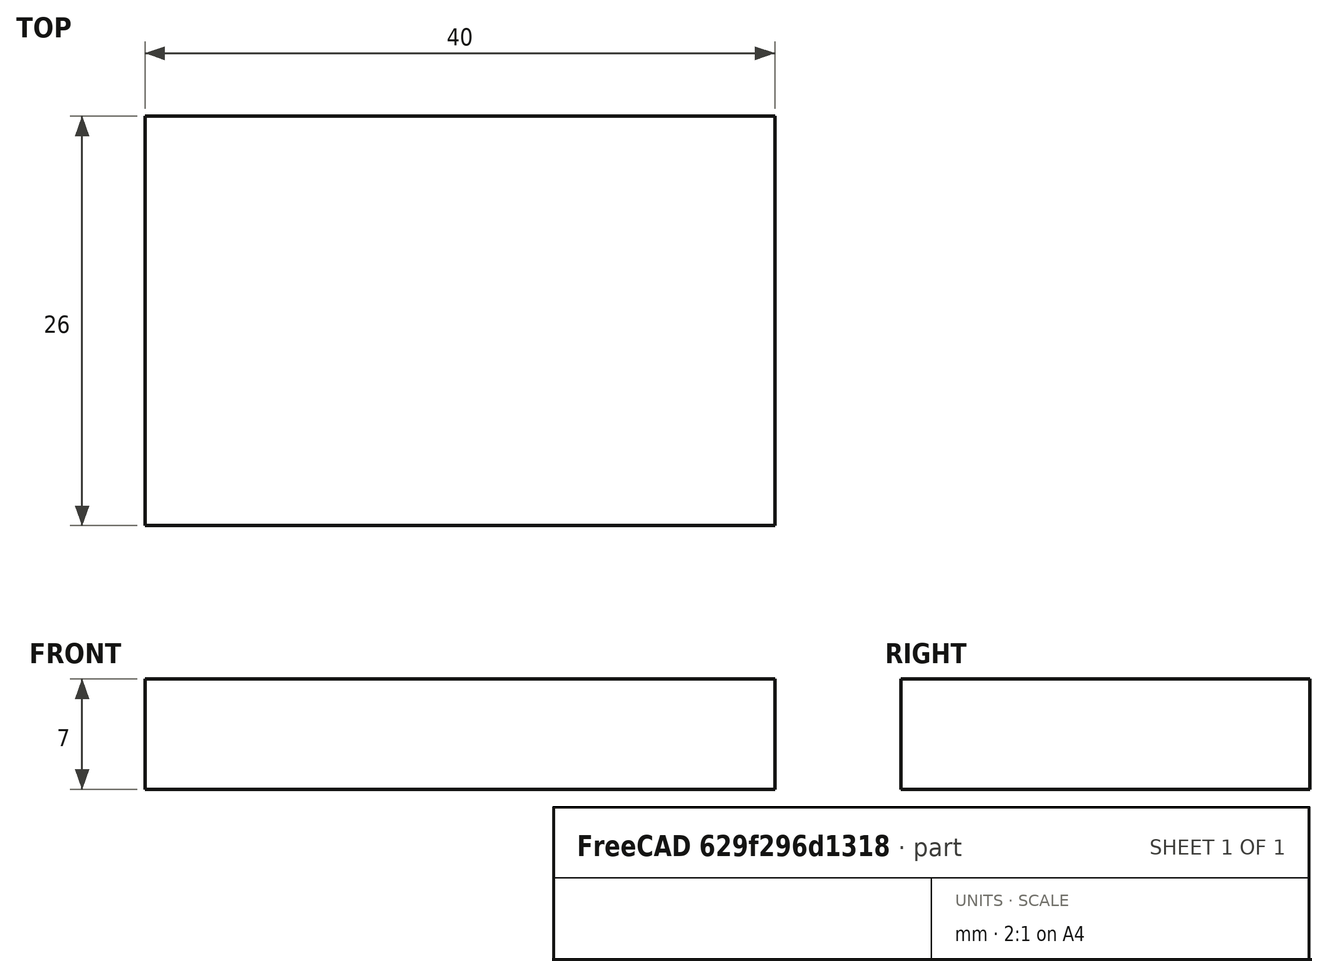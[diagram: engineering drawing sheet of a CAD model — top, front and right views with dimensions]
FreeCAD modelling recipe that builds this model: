
FCSTD DOCUMENT  (FreeCAD 0.17RUnknown)
Label: cam_tail
License: All rights reserved
LicenseURL: http://en.wikipedia.org/wiki/All_rights_reserved
objects: Path::FeaturePython×6, Part::FeaturePython×3, App::FeaturePython×1, Path::FeatureCompoundPython×1
note: 6 computed .brp shape members not serialized (recipe doc carries the construction recipe); baked Part::Feature solids carry a one-line shape summary decoded from their .brp

FEATURE [Path::FeaturePython] Default_Tool  label="Default Tool"  # Path/CAM operation (typed FeaturePython)
  HorizFeed = 3.33333
  HorizRapid = 0
  SpindleDir = 0
  SpindleSpeed = 12000
  ToolNumber = 1
  VertFeed = 1.33333
  VertRapid = 0
  expr: Tool.Diameter = 2
  expr: VertFeed = 80mm / min
  expr: HorizFeed = 200mm / min
  expr: HorizRapid = SetupSheet.HorizRapid
  expr: VertRapid = SetupSheet.VertRapid
FEATURE [Path::FeaturePython] Contour  # Path/CAM operation (typed FeaturePython)
  Active = true
  AreaParams:
    OpenMode = 0
    Angle = 45.0
    MinArcPoints = 4
    Coplanar = 2
    Tolerance = 1e-07
    CleanDistance = 0.0
    PocketExtraOffset = 0.0
    RoundPrecision = 0.0
    AngleShift = 0.0
    SubjectFill = 0
    PocketMode = 0
    Simplify = False
    SectionTolerance = 1e-06
    MaxArcPoints = 100
    Offset = 1.0
    Accuracy = 0.01
    PocketStepover = 0.0
    ClipFill = 0
    ToolRadius = 1.0
    Outline = False
    ClipperScale = 10000000.0
    FromCenter = False
    Explode = False
    EndType = 0
    Shift = 0.0
    ExtraPass = 0
    Project = False
    JoinType = 0
    Thicken = False
    Stepdown = 1.0
    SectionMode = 2
    MiterLimit = 2.0
    Deflection = 0.01
    Reorient = True
    FitArcs = True
    SectionCount = -1
    SectionOffset = 0.0
    Stepover = 0.0
    Unit = 1.0
    Fill = 0
  ClearanceHeight = 2
  Direction = 0
  FinalDepth = -6
  JoinType = 0
  MiterLimit = 0.1
  OffsetExtra = 0
  OpFinalDepth = -7
  OpStartDepth = 0
  OpToolDiameter = 2
  PathParams:
    resume_height = 2.0000000000000053
    feedrate = 3.3333333333333335
    verbose = True
    orientation = 1
    return_end = True
    preamble = False
    retraction = 2.0000000000000053
    feedrate_v = 1.3333333333333333
  SafeHeight = 2
  Side = 0
  StartDepth = 0
  StartPoint = (0,0,0)
  StepDown = 0.1
  ToolController = -> Default_Tool
  UseComp = true
  UseStartPoint = false
  expr: FinalDepth = -6
  expr: ClearanceHeight = StartDepth + SetupSheet.ClearanceHeightOffset
  expr: SafeHeight = StartDepth + SetupSheet.SafeHeightOffset
  expr: StepDown = 0.10000000000000001
  expr: StartDepth = OpStartDepth
FEATURE [App::FeaturePython] SetupSheet  # Path/CAM operation (typed FeaturePython)
  ClearanceHeightExpression = StartDepth+SetupSheet.ClearanceHeightOffset
  ClearanceHeightOffset = 2
  FinalDepthExpression = OpFinalDepth
  HorizRapid = 0
  SafeHeightExpression = StartDepth+SetupSheet.SafeHeightOffset
  SafeHeightOffset = 2
  StartDepthExpression = OpStartDepth
  StepDownExpression = OpToolDiameter
  VertRapid = 0
FEATURE [Part::FeaturePython] tail_01  # a2plus imported part (geometry in sourceFile) (typed FeaturePython)
  fixedPosition = true
  sourceFile = <userpath>/hs/fly/cad/tail.fcstd
  timeLastImport = 1.53696e+09
  updateColors = true
FEATURE [Part::FeaturePython] Clone  label="Base-arm_01"  # Draft clone (typed FeaturePython)
  AttacherType = Attacher::AttachEngine3D
  Fuse = false
  Objects = -> [tail_01]
  PathResource = Base
  Placement = pos=(21,17,-2.5) rot=(1,0,0;-1.5708rad)
  Scale = (1,1,1)
FEATURE [Path::FeaturePython] Pocket_Shape  # Path/CAM operation (typed FeaturePython)
  Active = true
  AreaParams:
    OpenMode = 0
    Angle = 45.0
    MinArcPoints = 4
    Coplanar = 0
    Tolerance = 1e-07
    CleanDistance = 0.0
    PocketExtraOffset = 0.0
    RoundPrecision = 0.0
    AngleShift = 0.0
    SubjectFill = 0
    PocketMode = 2
    Simplify = False
    SectionTolerance = 1e-06
    MaxArcPoints = 100
    Offset = 0.0
    Accuracy = 0.01
    PocketStepover = 1.0
    ClipFill = 0
    ToolRadius = 1.0
    Outline = False
    ClipperScale = 10000000.0
    FromCenter = True
    Explode = False
    EndType = 0
    Shift = 0.0
    ExtraPass = 0
    Project = False
    JoinType = 0
    Thicken = False
    Stepdown = 1.0
    SectionMode = 2
    MiterLimit = 2.0
    Deflection = 0.01
    Reorient = True
    FitArcs = True
    SectionCount = -1
    SectionOffset = 0.0
    Stepover = 0.0
    Unit = 1.0
    Fill = 0
  Base = -> [Clone]
  ClearanceHeight = 2
  CutMode = 0
  ExtraOffset = 0
  FinalDepth = -3
  FinishDepth = 0
  KeepToolDown = false
  MinTravel = false
  OffsetPattern = 1
  OpFinalDepth = -3
  OpStartDepth = 0
  OpToolDiameter = 2
  PathParams = {'resume_height': 2.0, 'feedrate': 3.3333333333333335, 'verbose': True, 'orientation': 1, 'return_end': True, 'preamble': False, 'retraction': 2.0, 'feedrate_v': 1.3333333333333333}
  SafeHeight = 2
  StartAt = 0
  StartDepth = 0
  StartPoint = (0,0,0)
  StepDown = 0.1
  StepOver = 50
  ToolController = -> Default_Tool
  UseStartPoint = false
  ZigZagAngle = 45
  expr: ClearanceHeight = StartDepth + SetupSheet.ClearanceHeightOffset
  expr: SafeHeight = StartDepth + SetupSheet.SafeHeightOffset
  expr: StepDown = 0.10000000000000001
  expr: FinalDepth = -3
  expr: StartDepth = 0
FEATURE [Part::FeaturePython] Stock  # WARN: FeaturePython — macro-defined, semantics opaque (R4)
  Base = -> tail_01
  ExtXneg = 1
  ExtXpos = 1
  ExtYneg = 1
  ExtYpos = 1
  ExtZneg = 1
  ExtZpos = 1
  Placement = pos=(21,17,-3.5) rot=(1,0,0;4.71239rad)
  StockType = FromBase
FEATURE [Path::FeaturePython] Pocket_Shape001  # Path/CAM operation (typed FeaturePython)
  Active = true
  AreaParams:
    OpenMode = 0
    Angle = 45.0
    MinArcPoints = 4
    Coplanar = 0
    Tolerance = 1e-07
    CleanDistance = 0.0
    PocketExtraOffset = 0.0
    RoundPrecision = 0.0
    AngleShift = 0.0
    SubjectFill = 0
    PocketMode = 2
    Simplify = False
    SectionTolerance = 1e-06
    MaxArcPoints = 100
    Offset = 0.0
    Accuracy = 0.01
    PocketStepover = 1.0
    ClipFill = 0
    ToolRadius = 1.0
    Outline = False
    ClipperScale = 10000000.0
    FromCenter = True
    Explode = False
    EndType = 0
    Shift = 0.0
    ExtraPass = 0
    Project = False
    JoinType = 0
    Thicken = False
    Stepdown = 1.0
    SectionMode = 2
    MiterLimit = 2.0
    Deflection = 0.01
    Reorient = True
    FitArcs = True
    SectionCount = -1
    SectionOffset = 0.0
    Stepover = 0.0
    Unit = 1.0
    Fill = 0
  Base = -> [Clone]
  ClearanceHeight = -1
  CutMode = 0
  ExtraOffset = 0
  FinalDepth = -6
  FinishDepth = 0
  KeepToolDown = false
  MinTravel = false
  OffsetPattern = 1
  OpFinalDepth = -5
  OpStartDepth = 0
  OpToolDiameter = 2
  PathParams = {'resume_height': -1.0, 'feedrate': 3.3333333333333335, 'verbose': True, 'orientation': 1, 'return_end': True, 'preamble': False, 'retraction': -1.0, 'feedrate_v': 1.3333333333333333}
  SafeHeight = -1
  StartAt = 0
  StartDepth = -3
  StartPoint = (0,0,0)
  StepDown = 0.1
  StepOver = 50
  ToolController = -> Default_Tool
  UseStartPoint = false
  ZigZagAngle = 45
  expr: ClearanceHeight = StartDepth + SetupSheet.ClearanceHeightOffset
  expr: SafeHeight = StartDepth + SetupSheet.SafeHeightOffset
  expr: StepDown = 0.10000000000000001
  expr: FinalDepth = -6
  expr: StartDepth = -3
FEATURE [Path::FeaturePython] TagDressup  # Path/CAM operation (typed FeaturePython)
  Angle = 45
  Base = -> Contour
  Height = 3
  Positions = (2) [(1,17.15,0),(41,16.59,0)]
  Radius = 0
  SegmentationFactor = 50
  Width = 3.8
FEATURE [Path::FeatureCompoundPython] Operations  # Path/CAM operation (typed FeaturePython)
  Group = -> [Pocket_Shape,Pocket_Shape001,TagDressup]
  UsePlacements = false
FEATURE [Path::FeaturePython] Job  # Path/CAM operation (typed FeaturePython)
  Base = -> Clone
  GeometryTolerance = 0.01
  Operations = -> Operations
  PostProcessor = 5
  PostProcessorOutputFile = <userpath>/hs/fly/cad/gcode/arm
  SetupSheet = -> SetupSheet
  Stock = -> Stock
  ToolController = -> [Default_Tool]
